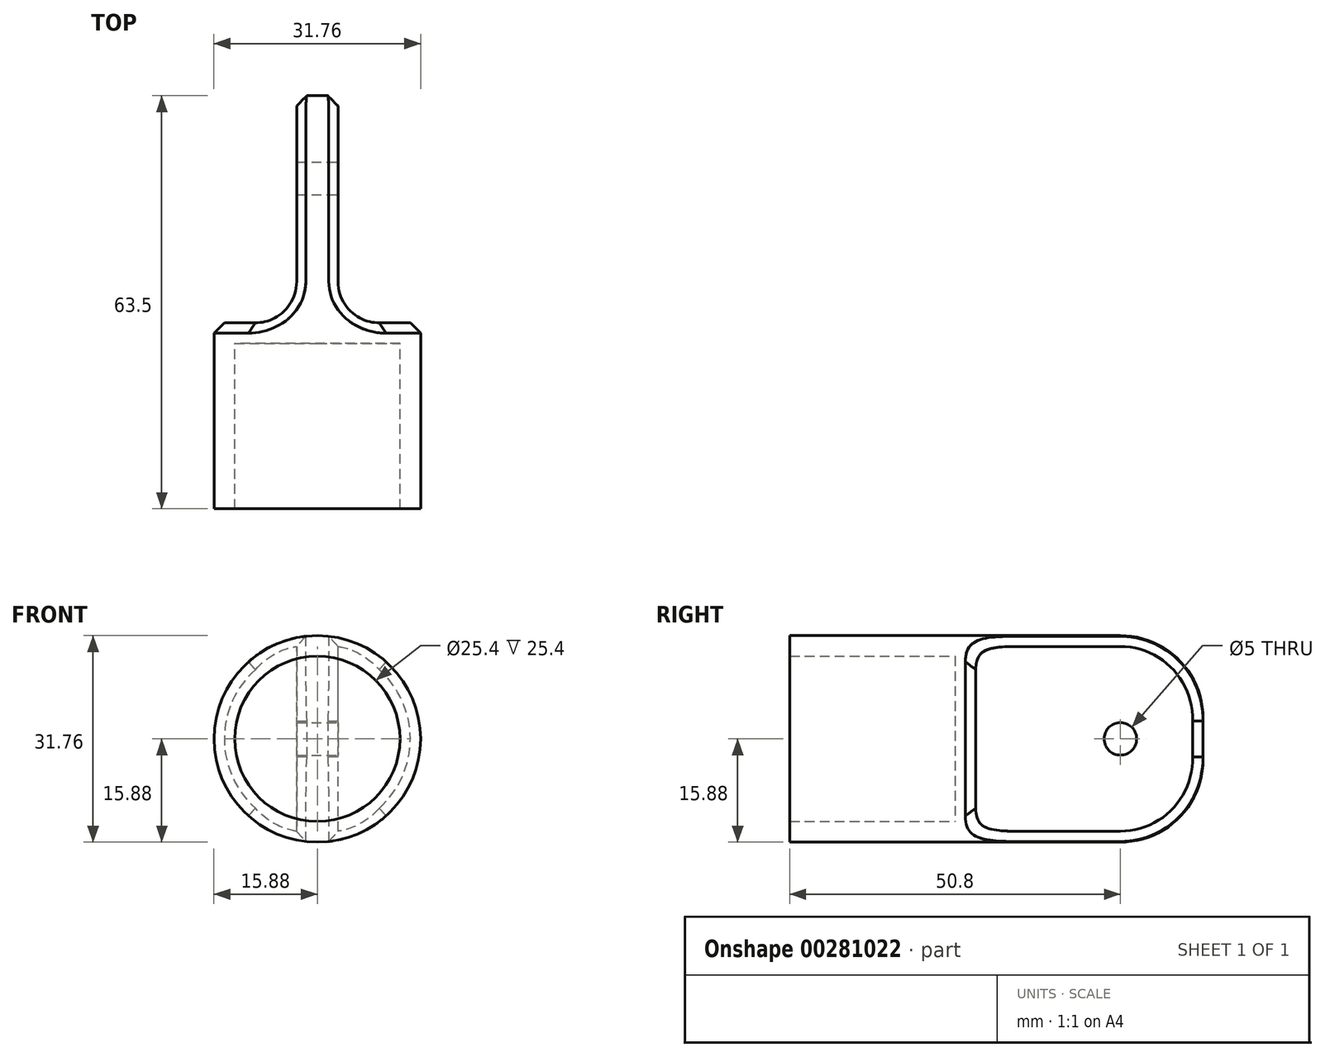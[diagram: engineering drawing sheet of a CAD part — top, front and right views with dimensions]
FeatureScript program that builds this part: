
annotation { "Feature Type Name" : "Feature", "Feature Type Description" : "" }
export const myFeature = defineFeature(function(context is Context, id is Id, definition is map)
    precondition{}
    {
        {
            var Q0;
            Q0=qCreatedBy(makeId("Top.planeOp"),FACE);
            var sketch = newSketch(context, id + "F0", { "sketchPlane" : qUnion([Q0])});
            skLineSegment(sketch, "E0", {"start": v(0, 0) * mm, "end": v(12.7, 0) * mm});
            skLineSegment(sketch, "E1", {"start": v(12.7, 0) * mm, "end": v(15.87, 0) * mm});
            skLineSegment(sketch, "E2", {"start": v(15.87, 0) * mm, "end": v(15.87, 63.5) * mm});
            skLineSegment(sketch, "E3", {"start": v(15.88, 63.5) * mm, "end": v(0, 63.5) * mm});
            skLineSegment(sketch, "E4", {"start": v(0, 63.5) * mm, "end": v(0, 25.4) * mm});
            skLineSegment(sketch, "E5", {"start": v(0, 25.4) * mm, "end": v(12.7, 25.4) * mm});
            skLineSegment(sketch, "E6", {"start": v(12.7, 25.4) * mm, "end": v(12.7, 0) * mm});
            skSolve(sketch);
        }
        {
            var Q0;
            Q0=makeQuery(id+"F0.imprint","IMPRINT",FACE,{"disambiguationData":[TD([[makeQuery(id+"F0.imprint","IMPRINT",EDGE,{"derivedFrom":sQuery(id+"F0.wireOp",EDGE,"E1")}),1.0]])]});
            var Q1;
            Q1=sQuery(id+"F0.wireOp",EDGE,"E4");
            revolve(context, id + "F1", {"entities" : qUnion([Q0]), "axis" : qUnion([Q1]), "revolveType" : RevolveType.FULL});
        }
        {
            var Q0;
            Q0=qCreatedBy(makeId("Right.planeOp"),FACE);
            var sketch = newSketch(context, id + "F2", { "sketchPlane" : qUnion([Q0])});
            skPoint(sketch, "E7.0", {"position": v(50.8, 0) * mm});
            skCircle(sketch, "E8", {"center": v(50.8, 0) * mm, "radius": 2.5 * mm});
            skSolve(sketch);
        }
        {
            var Q0;
            Q0 = qSketchRegion(id + "F2", true);
            extrude(context, id + "F3", {"entities" : qUnion([Q0]), "operationType" : NewBodyOperationType.REMOVE, "endBound" : BoundingType.SYMMETRIC, "oppositeDirection" : true, "depth" : 50.8 * mm});
        }
        {
            var Q0;
            Q0=qCreatedBy(makeId("Top.planeOp"),FACE);
            var sketch = newSketch(context, id + "F4", { "sketchPlane" : qUnion([Q0])});
            skLineSegment(sketch, "E9.0", {"start": v(0, 63.5) * mm, "end": v(0, 25.4) * mm, "construction": true});
            skLineSegment(sketch, "E10", {"start": v(0, 63.5) * mm, "end": v(4.74, 63.5) * mm, "construction": true});
            skLineSegment(sketch, "E11", {"start": v(3.18, 63.5) * mm, "end": v(3.18, 34.92) * mm});
            skLineSegment(sketch, "E12.0", {"start": v(15.87, 0) * mm, "end": v(15.87, 63.5) * mm});
            skLineSegment(sketch, "E13", {"start": v(3.18, 63.5) * mm, "end": v(15.87, 63.5) * mm});
            skLineSegment(sketch, "E14", {"start": v(15.87, 63.5) * mm, "end": v(15.87, 28.57) * mm});
            skLineSegment(sketch, "E15.MirrorCS", {"start": v(-3.17, 63.5) * mm, "end": v(-3.18, 34.92) * mm});
            skLineSegment(sketch, "E16.MirrorCS", {"start": v(-3.18, 63.5) * mm, "end": v(-15.87, 63.5) * mm});
            skLineSegment(sketch, "E17", {"start": v(15.87, 28.57) * mm, "end": v(9.53, 28.57) * mm});
            skPoint(sketch, "E18.visualSharp", {"position": v(3.18, 28.57) * mm});
            skArc(sketch, "E18.filletArc", {"start": v(3.17, 34.92) * mm, "mid": v(5.03, 30.43) * mm, "end": v(9.53, 28.57) * mm});
            skArc(sketch, "E19.MirrorCS", {"start": v(-3.17, 34.92) * mm, "mid": v(-5.03, 30.43) * mm, "end": v(-9.53, 28.57) * mm});
            skLineSegment(sketch, "E20.MirrorCS", {"start": v(-15.87, 28.57) * mm, "end": v(-9.53, 28.57) * mm});
            skPoint(sketch, "E21.orphan", {"position": v(-3.18, 28.57) * mm});
            skLineSegment(sketch, "E22.MirrorCS", {"start": v(-15.87, 63.5) * mm, "end": v(-15.87, 28.57) * mm});
            skSolve(sketch);
        }
        {
            var Q0;
            Q0 = qSketchRegion(id + "F4", true);
            extrude(context, id + "F5", {"entities" : qUnion([Q0]), "operationType" : NewBodyOperationType.REMOVE, "endBound" : BoundingType.UP_TO_NEXT, "oppositeDirection" : true, "depth" : 25.4 * mm, "hasSecondDirection" : true, "secondDirectionOppositeDirection" : false, "secondDirectionDepth" : 25.4 * mm});
        }
        {
            var Q0;
            Q0=makeQuery(id+"F5.boolean.opBoolean","SPLIT",EDGE,{"disambiguationData":[OD(1.0)],"derivedFrom":makeQuery(id+"F1.opRevolve","SWEPT_EDGE",EDGE,{"disambiguationData":[OSD([sQuery(id+"F0.wireOp",EDGE,"E2"),sQuery(id+"F0.wireOp",EDGE,"E3")])]})});
            var Q1;
            Q1=makeQuery(id+"F5.boolean.opBoolean","SPLIT",EDGE,{"disambiguationData":[OD(0.0)],"derivedFrom":makeQuery(id+"F1.opRevolve","SWEPT_EDGE",EDGE,{"disambiguationData":[OSD([sQuery(id+"F0.wireOp",EDGE,"E2"),sQuery(id+"F0.wireOp",EDGE,"E3")])]})});
            fillet(context, id + "F6", {"entities" : qUnion([Q0, Q1]), "radius" : 12.7 * mm, "tangentPropagation" : true, "allowEdgeOverflow" : false});
        }
        {
            var Q0;
            Q0=makeQuery(id+"F5.boolean.opBoolean","COPY",EDGE,{"derivedFrom":makeQuery(id+"F5.opExtrude","TWEAK_EDGE",EDGE,{"disambiguationData":[OD(0.0)],"derivedFrom":[makeQuery(id+"F1.opRevolve","SWEPT_FACE",FACE,{"disambiguationData":[OSD([sQuery(id+"F0.wireOp",EDGE,"E2")])]}),makeQuery(id+"F4.imprint","IMPRINT",EDGE,{"derivedFrom":sQuery(id+"F4.wireOp",EDGE,"E15.MirrorCS")})]})});
            var Q1;
            {var subQ0=makeQuery(id+"F4.imprint","IMPRINT",EDGE,{"derivedFrom":sQuery(id+"F4.wireOp",EDGE,"E20.MirrorCS")});var subQ1=makeQuery(id+"F1.opRevolve","SWEPT_FACE",FACE,{"disambiguationData":[OSD([sQuery(id+"F0.wireOp",EDGE,"E2")])]});Q1=makeQuery(id+"F5.boolean.opBoolean","TWEAK_EDGE",EDGE,{"derivedFrom":[makeQuery(id+"F5.opExtrude","TWEAK_EDGE",EDGE,{"disambiguationData":[OD(0.0)],"derivedFrom":[subQ1,subQ0]}),makeQuery(id+"F5.opExtrude","TWEAK_EDGE",EDGE,{"disambiguationData":[OD(1.0)],"derivedFrom":[subQ1,subQ0]})]});}
            var Q2;
            Q2=makeQuery(id+"F6.opFillet","BLEND_EDGE",EDGE,{"blendedFrom":[makeQuery(id+"F5.boolean.opBoolean","SPLIT",EDGE,{"disambiguationData":[OD(1.0)],"derivedFrom":makeQuery(id+"F1.opRevolve","SWEPT_EDGE",EDGE,{"disambiguationData":[OSD([sQuery(id+"F0.wireOp",EDGE,"E2"),sQuery(id+"F0.wireOp",EDGE,"E3")])]})}),makeQuery(id+"F5.boolean.opBoolean","COPY",FACE,{"derivedFrom":makeQuery(id+"F5.opExtrude","SWEPT_FACE",FACE,{"disambiguationData":[OSD([sQuery(id+"F4.wireOp",EDGE,"E15.MirrorCS")])]})})],"blendedInto":[makeQuery(id+"F5.boolean.opBoolean","COPY",FACE,{"derivedFrom":makeQuery(id+"F5.opExtrude","SWEPT_FACE",FACE,{"disambiguationData":[OSD([sQuery(id+"F4.wireOp",EDGE,"E15.MirrorCS")])]})})]});
            var Q3;
            Q3=makeQuery(id+"F6.opFillet","BLEND_EDGE",EDGE,{"blendedFrom":[makeQuery(id+"F5.boolean.opBoolean","SPLIT",EDGE,{"disambiguationData":[OD(0.0)],"derivedFrom":makeQuery(id+"F1.opRevolve","SWEPT_EDGE",EDGE,{"disambiguationData":[OSD([sQuery(id+"F0.wireOp",EDGE,"E2"),sQuery(id+"F0.wireOp",EDGE,"E3")])]})}),makeQuery(id+"F5.boolean.opBoolean","COPY",FACE,{"derivedFrom":makeQuery(id+"F5.opExtrude","SWEPT_FACE",FACE,{"disambiguationData":[OSD([sQuery(id+"F4.wireOp",EDGE,"E11")])]})})],"blendedInto":[makeQuery(id+"F5.boolean.opBoolean","COPY",FACE,{"derivedFrom":makeQuery(id+"F5.opExtrude","SWEPT_FACE",FACE,{"disambiguationData":[OSD([sQuery(id+"F4.wireOp",EDGE,"E11")])]})})]});
            chamfer(context, id + "F7", {"entities" : qUnion([Q0, Q1, Q2, Q3]), "width" : 1.59 * mm, "tangentPropagation" : true});
        }
    });
